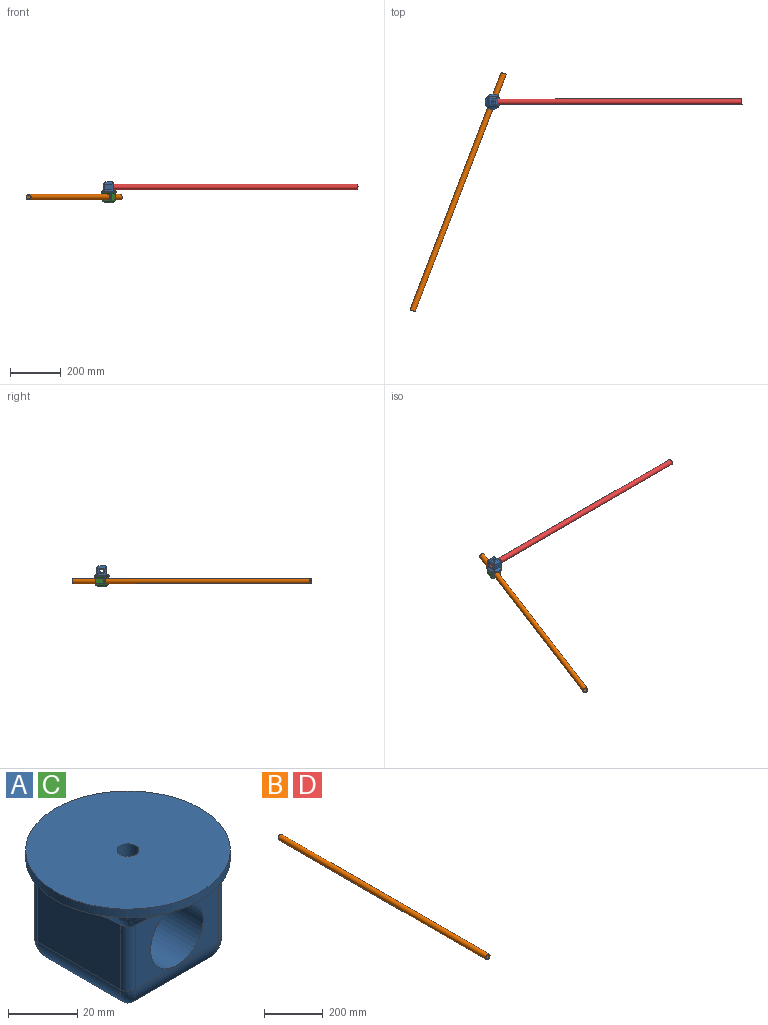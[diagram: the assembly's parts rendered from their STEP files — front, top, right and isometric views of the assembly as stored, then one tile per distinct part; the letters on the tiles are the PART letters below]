
ASSEMBLY  parts=4 mates=3
PART A: 44 faces, bbox 60.2x60.2x41 mm
  f0: plane 22x22mm, normal (0,0,-1), area 369.5mm2, adj f12,f15,f16,f19,f21,f22,f23,f24
  f1: cylinder r=3.17mm len=6.35mm, axis (0,0,1), area 94.4mm2, adj f3,f20
  f2: plane 34x23mm, normal (1,0,0), area 782mm2, adj f9,f11,f19,f34
  f3: cylinder r=10.75mm len=40mm, axis (0,1,0), area 2640.6mm2, adj f1,f5,f6,f7
  f4: plane 34x23mm, normal (-1,0,0), area 782mm2, adj f8,f10,f12,f32
  f5: plane 34x23mm, normal (0,-1,0), area 418.9mm2, adj f3,f10,f11,f15,f33
  f6: plane 34x23mm, normal (0,1,0), area 418.9mm2, adj f3,f8,f9,f16,f31
  f7: cylinder r=3.17mm len=9.73mm, axis (0,0,1), area 189.3mm2, adj f3,f39
  f8: cylinder r=3mm len=23mm, axis (0,0,-1), area 108.4mm2, adj f4,f6,f14,f27
  f9: cylinder r=3mm len=23mm, axis (0,0,1), area 108.4mm2, adj f2,f6,f18,f30
  f10: cylinder r=3mm len=23mm, axis (0,0,1), area 108.4mm2, adj f4,f5,f13,f28
  f11: cylinder r=3mm len=23mm, axis (0,0,-1), area 108.4mm2, adj f2,f5,f17,f29
  f12: cylinder r=9mm len=34mm, axis (0,1,0), area 395.8mm2, adj f0,f4,f13,f14
  f13: bspline ~9.39x9mm, area 29.2mm2, adj f10,f12,f15
  f14: bspline ~9.39x9mm, area 29.2mm2, adj f8,f12,f16
  f15: cylinder r=9mm len=34mm, axis (-1,0,0), area 395.8mm2, adj f0,f5,f13,f17
  f16: cylinder r=9mm len=34mm, axis (1,0,0), area 395.8mm2, adj f0,f6,f14,f18
  f17: bspline ~9.39x9mm, area 29.2mm2, adj f11,f15,f19
  f18: bspline ~9.39x9mm, area 29.2mm2, adj f9,f16,f19
  f19: cylinder r=9mm len=34mm, axis (0,-1,0), area 395.8mm2, adj f0,f2,f17,f18
  f20: plane 13.28x11.5mm, normal (0,0,-1), area 82.9mm2, adj f1,f21,f22,f23,f24,f25,f26
  f21: plane 5.75x5mm, normal (0.5,-0.87,0), area 33.2mm2, adj f0,f20,f22,f26
  f22: plane 5.75x5mm, normal (-0.5,-0.87,0), area 33.2mm2, adj f0,f20,f21,f23
  f23: plane 6.64x5mm, normal (-1,0,0), area 33.2mm2, adj f0,f20,f22,f24
  f24: plane 5.75x5mm, normal (-0.5,0.87,0), area 33.2mm2, adj f0,f20,f23,f25
  f25: plane 5.75x5mm, normal (0.5,0.87,0), area 33.2mm2, adj f0,f20,f24,f26
  f26: plane 6.64x5mm, normal (1,0,0), area 33.2mm2, adj f0,f20,f21,f25
  f27: plane 4.02x4.02mm, normal (0,0,-1), area 0.6mm2, adj f8,f31,f32,f42
  f28: plane 4.02x4.02mm, normal (0,0,-1), area 0.6mm2, adj f10,f32,f33,f41
  f29: plane 4.02x4.02mm, normal (0,0,-1), area 0.6mm2, adj f11,f33,f34,f40
  f30: plane 4.02x4.02mm, normal (0,0,-1), area 0.6mm2, adj f9,f31,f34,f43
  f31: bspline ~41.85x9.59mm, area 352.5mm2, adj f6,f27,f30,f36,f42,f43
  f32: bspline ~41.85x9.59mm, area 352.5mm2, adj f4,f27,f28,f37,f41,f42
  f33: bspline ~41.85x9.59mm, area 352.5mm2, adj f5,f28,f29,f38,f40,f41
  f34: bspline ~41.85x9.59mm, area 352.5mm2, adj f2,f29,f30,f35,f40,f43
  f35: extruded ~41.85x8.67mm, area 139.4mm2, adj f34,f36,f38,f39
  f36: extruded ~41.85x8.67mm, area 139.4mm2, adj f31,f35,f37,f39
  f37: extruded ~41.85x8.67mm, area 139.4mm2, adj f32,f36,f38,f39
  f38: extruded ~41.85x8.67mm, area 139.4mm2, adj f33,f35,f37,f39
  f39: plane 59.18x59.18mm, normal (0,0,1), area 2719.4mm2, adj f7,f35,f36,f37,f38
  f40: bspline ~6.78x4.15mm, area 8.8mm2, adj f29,f33,f34
  f41: bspline ~6.78x4.15mm, area 8.8mm2, adj f28,f32,f33
  f42: bspline ~6.78x4.15mm, area 8.8mm2, adj f27,f31,f32
  f43: bspline ~6.78x4.15mm, area 8.8mm2, adj f30,f31,f34
PART B: 4 faces, bbox 21.5x1000x21.5 mm
  f0: cylinder r=7.75mm len=1000mm, axis (0,1,0), area 48694.7mm2, adj f2,f3
  f1: cylinder r=10.75mm len=1000mm, axis (0,1,0), area 67544.2mm2, adj f2,f3
  f2: plane 21.5x21.5mm, normal (0,-1,0), area 174.4mm2, adj f0,f1
  f3: plane 21.5x21.5mm, normal (0,1,0), area 174.4mm2, adj f0,f1
PART C: same geometry as A
PART D: same geometry as B
PLACE A rot(axis=(-0.71,0.71,0),180deg) t=(36.72,0,39.83)mm fixed
PLACE B rot(axis=(0,0,-1),21deg) t=(-99.45,-354.76,-0.17)mm
PLACE C rot(axis=(0,0,-1),21deg) t=(36.72,0,-0.17)mm
PLACE D rot(axis=(0,0,-1),90deg) t=(516.72,0.18,39.83)mm
MATE revolute C.f1 <-> A.f1  axis (0,0,1) through (36.72,0,19.83)mm
MATE fastened B.f0 <-> C.f3  axis (0.36,0.93,0) through (43.89,18.67,-0.17)mm
MATE fastened A.f3 <-> D.f0  axis (-1,0,0) through (16.72,-0.01,39.83)mm
